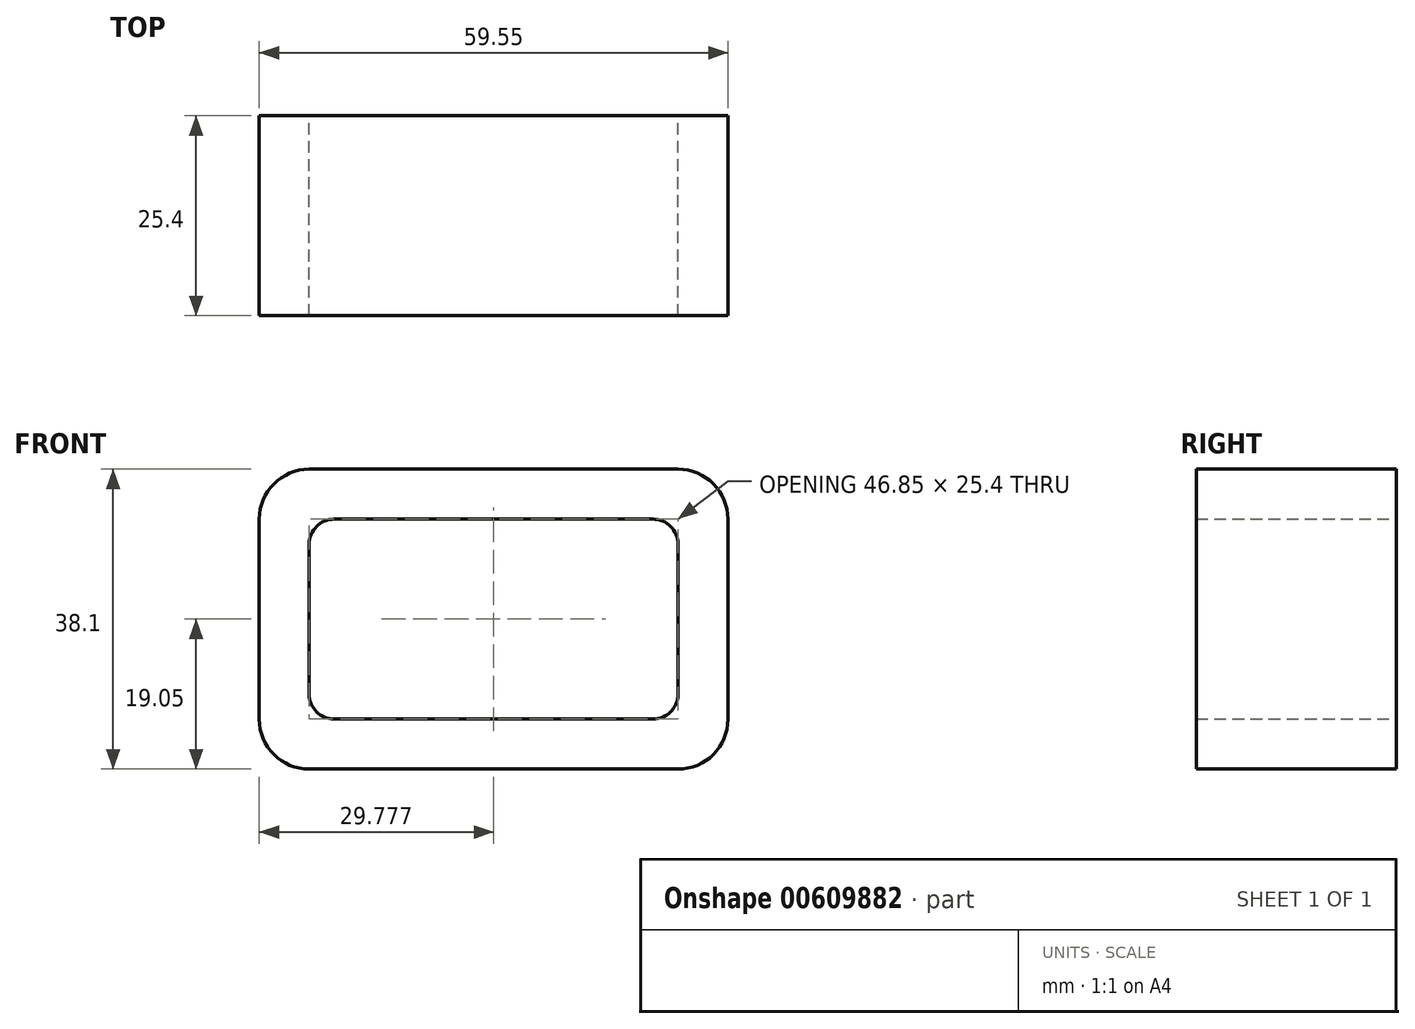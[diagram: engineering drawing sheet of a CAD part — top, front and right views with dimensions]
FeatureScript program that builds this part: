
annotation { "Feature Type Name" : "Feature", "Feature Type Description" : "" }
export const myFeature = defineFeature(function(context is Context, id is Id, definition is map)
    precondition{}
    {
        {
            var Q0;
            Q0=qCreatedBy(makeId("Front.planeOp"),FACE);
            var sketch = newSketch(context, id + "F0", { "sketchPlane" : qUnion([Q0])});
            skLineSegment(sketch, "E0", {"start": v(0, 6.35) * mm, "end": v(0, 31.75) * mm});
            skLineSegment(sketch, "E1", {"start": v(-6.35, 38.1) * mm, "end": v(-53.2, 38.1) * mm});
            skLineSegment(sketch, "E2", {"start": v(-59.55, 31.75) * mm, "end": v(-59.55, 6.35) * mm});
            skLineSegment(sketch, "E3", {"start": v(-53.2, 0) * mm, "end": v(-6.35, 0) * mm});
            skLineSegment(sketch, "E4.bottom", {"start": v(-50.02, 31.75) * mm, "end": v(-9.52, 31.75) * mm});
            skLineSegment(sketch, "E4.top", {"start": v(-50.02, 6.35) * mm, "end": v(-9.52, 6.35) * mm});
            skLineSegment(sketch, "E4.left", {"start": v(-53.2, 28.58) * mm, "end": v(-53.2, 9.52) * mm});
            skLineSegment(sketch, "E4.right", {"start": v(-6.35, 28.58) * mm, "end": v(-6.35, 9.53) * mm});
            skPoint(sketch, "E5.visualSharp", {"position": v(-59.55, 38.1) * mm});
            skArc(sketch, "E5.filletArc", {"start": v(-53.2, 38.1) * mm, "mid": v(-57.69, 36.24) * mm, "end": v(-59.55, 31.75) * mm});
            skPoint(sketch, "E6.visualSharp", {"position": v(-59.55, 0) * mm});
            skArc(sketch, "E6.filletArc", {"start": v(-59.55, 6.35) * mm, "mid": v(-57.69, 1.86) * mm, "end": v(-53.2, 0) * mm});
            skPoint(sketch, "E7.visualSharp", {"position": v(0, 0) * mm});
            skArc(sketch, "E7.filletArc", {"start": v(-6.35, 0) * mm, "mid": v(-1.86, 1.86) * mm, "end": v(0, 6.35) * mm});
            skPoint(sketch, "E8.visualSharp", {"position": v(0, 38.1) * mm});
            skArc(sketch, "E8.filletArc", {"start": v(0, 31.75) * mm, "mid": v(-1.86, 36.24) * mm, "end": v(-6.35, 38.1) * mm});
            skArc(sketch, "E9.filletArc", {"start": v(-6.35, 28.58) * mm, "mid": v(-7.28, 30.82) * mm, "end": v(-9.52, 31.75) * mm});
            skArc(sketch, "E10.filletArc", {"start": v(-9.52, 6.35) * mm, "mid": v(-7.28, 7.28) * mm, "end": v(-6.35, 9.53) * mm});
            skArc(sketch, "E11.filletArc", {"start": v(-53.2, 9.52) * mm, "mid": v(-52.27, 7.28) * mm, "end": v(-50.02, 6.35) * mm});
            skArc(sketch, "E12.filletArc", {"start": v(-50.02, 31.75) * mm, "mid": v(-52.27, 30.82) * mm, "end": v(-53.2, 28.58) * mm});
            skSolve(sketch);
        }
        {
            var Q0;
            Q0 = qSketchRegion(id + "F0", true);
            extrude(context, id + "F1", {"entities" : qUnion([Q0]), "depth" : 25.4 * mm, "offsetDistance" : 25.4 * mm});
        }
    });
